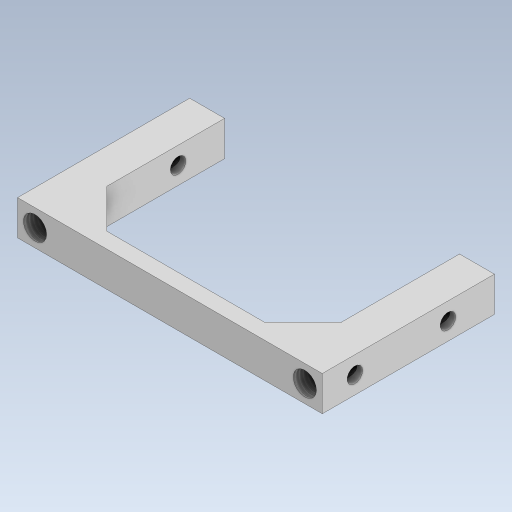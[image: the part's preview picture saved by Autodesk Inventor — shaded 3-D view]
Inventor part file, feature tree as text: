
AUTODESK INVENTOR PART (.ipt)
format: ipt  version: 2023.5 (Build 275446000, 446)  size: 371,712 bytes
history: native  units: in
note: dims shown in document units (in); Inventor stores cm internally (conversion verified against a paired STEP export)
features: extrude x6, sketch x5, plane x2, thread x2
ambient origin geometry x8: Origin, YZ Plane, XZ Plane, XY Plane, X Axis, Y Axis, Z Axis, Center Point
bodies: Solid1 (feature_tree)
feature tree (15):
  sketch  "Sketch1"  dims[d0=0.1181in d1=0.685in]
  extrude  "Extrusion1"  Depth=0.685in
  extrude  "Extrusion2"  Depth=0.1772in
  plane  "Work Plane1"
  extrude  "Extrusion3"  Depth=0.874in TaperAngle=0.0deg
  plane  "Work Plane2"
  extrude  "Extrusion4"  Depth=0.1969in
  extrude  "Extrusion5"  Depth=0.1969in
  thread  "Thread1"  [1 undecoded]
  thread  "Thread2"  [1 undecoded]
  extrude  "Extrusion6"  Depth=0.874in TaperAngle=0.0deg
  sketch  "Sketch2"  dims[d2=0.1772in d3=0.1772in]
  sketch  "Sketch5"  dims[d4=0.7953in d5=0.0in d6=0.874in d7=0.0in]
  sketch  "Sketch6"  dims[d8=0.0787in d9=0.0in d10=0.1969in]
  sketch  "Sketch7"  dims[d11=0.1969in d12=0.1969in d13=0.1772in d14=0.0in d15=0.0787in d16=0.0in d17=0.874in d18=0.0in d19=0.874in d20=0.0in d21=0.0787in d22=0.2362in d23=0.0787in d24=0.4724in d25=1.5748in d26=0.0in]
note: 2 required parameter values undecoded (feature->parameter linkage not recoverable at this tier; creation-order binding heuristic only, values carry confidence <= 0.55)
